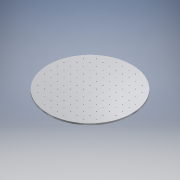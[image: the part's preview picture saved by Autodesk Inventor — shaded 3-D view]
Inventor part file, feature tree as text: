
AUTODESK INVENTOR PART (.ipt)
format: ipt  version: 2016 (Build 200138000, 138)  size: 256,000 bytes
history: native  units: mm
features: mirror x2, sketch x2, extrude x1, hole x1, chamfer x1
ambient origin geometry x8: Origin, YZ Plane, XZ Plane, XY Plane, X Axis, Y Axis, Z Axis, Center Point
bodies: Solid1 (feature_tree)
feature tree (7):
  extrude  "Extrusion1"  Depth=12.7mm TaperAngle=0.0deg
  hole  "Hole1"  [1 undecoded]
  mirror  "Mirror1"
  mirror  "Mirror2"
  chamfer  "Chamfer1"  Distance=60.0mm
  sketch  "Sketch1"  dims[d0=645.0mm d1=12.7mm d2=0.0mm]
  sketch  "Sketch2"  dims[d3=25.0mm d4=25.0mm d5=60.0mm d7=50.0mm d8=20.0mm d10=50.0mm d13=50.0mm d14=30.0mm d16=50.0mm d17=30.0mm d19=50.0mm d22=50.0mm d23=4.917mm d24=12.0mm d25=4.0mm d26=2.0mm d27=90.0deg d28=8.0mm d29=20.594885mm d30=0.5mm d31=2.0mm d32=45.0deg]
note: 1 required parameter value undecoded (feature->parameter linkage not recoverable at this tier; creation-order binding heuristic only, values carry confidence <= 0.55)
